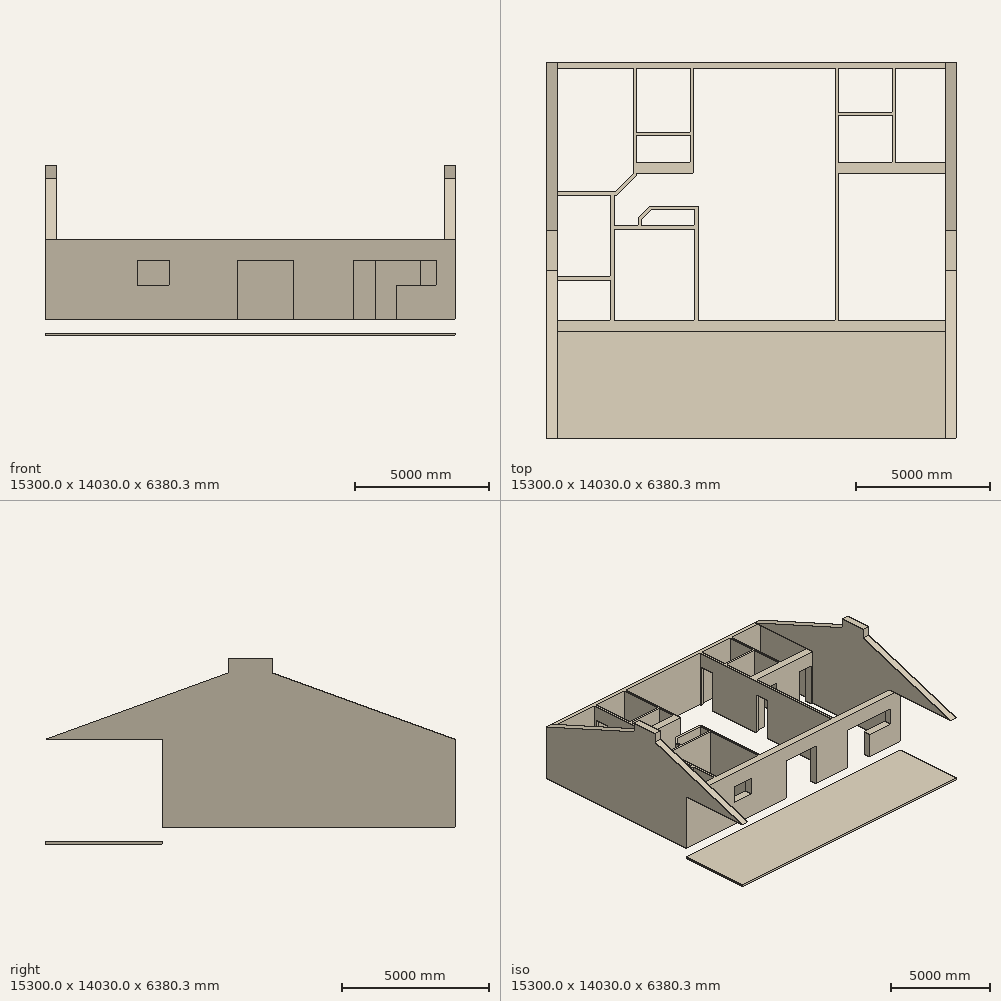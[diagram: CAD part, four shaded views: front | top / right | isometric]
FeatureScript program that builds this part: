
annotation { "Feature Type Name" : "Feature", "Feature Type Description" : "" }
export const myFeature = defineFeature(function(context is Context, id is Id, definition is map)
    precondition{}
    {
        {
            var Q0;
            Q0=qCreatedBy(makeId("Top.planeOp"),FACE);
            var sketch = newSketch(context, id + "F0", { "sketchPlane" : qUnion([Q0])});
            skLineSegment(sketch, "E0.left", {"start": v(-400, 5900) * mm, "end": v(-400, 400) * mm});
            skLineSegment(sketch, "E0.right", {"start": v(-14900, 6300) * mm, "end": v(-14900, 5200) * mm});
            skLineSegment(sketch, "E1.top", {"start": v(0, 0) * mm, "end": v(-6035, 0) * mm});
            skLineSegment(sketch, "E1.right", {"start": v(-15300, 6300) * mm, "end": v(-15300, 0) * mm});
            skLineSegment(sketch, "E2", {"start": v(0, 0) * mm, "end": v(0, 10030) * mm});
            skLineSegment(sketch, "E3", {"start": v(0, 10030) * mm, "end": v(-15300, 10030) * mm});
            skLineSegment(sketch, "E4", {"start": v(-15300, 10030) * mm, "end": v(-15300, 6300) * mm});
            skLineSegment(sketch, "E5", {"start": v(-15070, 6300) * mm, "end": v(-15070, 9800) * mm});
            skLineSegment(sketch, "E6", {"start": v(-230, 9800) * mm, "end": v(-230, 6300) * mm});
            skLineSegment(sketch, "E7.trimOffspring", {"start": v(-400, 5900) * mm, "end": v(-500, 5900) * mm});
            skLineSegment(sketch, "E8.trimOffspring", {"start": v(-230, 6300) * mm, "end": v(-500, 6300) * mm});
            skLineSegment(sketch, "E9.trimOffspring", {"start": v(-400, 400) * mm, "end": v(-4400, 400) * mm});
            skLineSegment(sketch, "E10", {"start": v(-15070, 9800) * mm, "end": v(-12070, 9800) * mm});
            skLineSegment(sketch, "E11", {"start": v(-4530, 400) * mm, "end": v(-4530, 5000) * mm});
            skLineSegment(sketch, "E12", {"start": v(-4400, 400) * mm, "end": v(-4400, 5000) * mm});
            skLineSegment(sketch, "E13", {"start": v(-2270, 6300) * mm, "end": v(-2270, 9800) * mm});
            skLineSegment(sketch, "E14", {"start": v(-2400, 6300) * mm, "end": v(-2400, 8050) * mm});
            skLineSegment(sketch, "E15", {"start": v(-4400, 6300) * mm, "end": v(-4400, 8050) * mm});
            skLineSegment(sketch, "E16", {"start": v(-4530, 5900) * mm, "end": v(-4530, 8900) * mm});
            skLineSegment(sketch, "E17", {"start": v(-4400, 8180) * mm, "end": v(-2400, 8180) * mm});
            skLineSegment(sketch, "E18", {"start": v(-4400, 8050) * mm, "end": v(-2400, 8050) * mm});
            skLineSegment(sketch, "E19", {"start": v(-12770, 400) * mm, "end": v(-12770, 500) * mm});
            skLineSegment(sketch, "E20", {"start": v(-12770, 3800) * mm, "end": v(-12670, 3800) * mm});
            skLineSegment(sketch, "E21", {"start": v(-9770, 3800) * mm, "end": v(-9770, 400) * mm});
            skLineSegment(sketch, "E22", {"start": v(-11940, 9800) * mm, "end": v(-11940, 9700) * mm});
            skLineSegment(sketch, "E23", {"start": v(-12070, 9800) * mm, "end": v(-12070, 9700) * mm});
            skLineSegment(sketch, "E24", {"start": v(-14900, 5070) * mm, "end": v(-12900, 5070) * mm});
            skLineSegment(sketch, "E25", {"start": v(-12652.55, 5070) * mm, "end": v(-12579.12, 5143.43) * mm});
            skLineSegment(sketch, "E26", {"start": v(-11940, 5782.55) * mm, "end": v(-11940, 5900) * mm});
            skLineSegment(sketch, "E27", {"start": v(-9640, 400) * mm, "end": v(-9640, 3930) * mm});
            skLineSegment(sketch, "E28", {"start": v(-9770, 3930) * mm, "end": v(-11740, 3930) * mm});
            skLineSegment(sketch, "E29", {"start": v(-12900, 3930) * mm, "end": v(-12900, 2030) * mm});
            skLineSegment(sketch, "E30", {"start": v(-9640, 3930) * mm, "end": v(-9640, 4660) * mm});
            skLineSegment(sketch, "E31", {"start": v(-9640, 4660) * mm, "end": v(-9780.34, 4660) * mm});
            skLineSegment(sketch, "E32", {"start": v(-11450.34, 4660) * mm, "end": v(-11870, 4240.34) * mm});
            skLineSegment(sketch, "E33", {"start": v(-11870, 4240.34) * mm, "end": v(-11870, 3800) * mm});
            skLineSegment(sketch, "E34", {"start": v(-11740, 3930) * mm, "end": v(-11740, 4186.5) * mm});
            skLineSegment(sketch, "E35", {"start": v(-11740, 4186.5) * mm, "end": v(-11396.5, 4530) * mm});
            skLineSegment(sketch, "E36", {"start": v(-11396.5, 4530) * mm, "end": v(-11380.34, 4530) * mm});
            skLineSegment(sketch, "E37", {"start": v(-9770, 4530) * mm, "end": v(-9770, 3930) * mm});
            skLineSegment(sketch, "E38", {"start": v(-12070, 6300) * mm, "end": v(-12070, 5836.4) * mm});
            skLineSegment(sketch, "E39", {"start": v(-12070, 5836.4) * mm, "end": v(-12105.36, 5801.04) * mm});
            skLineSegment(sketch, "E40", {"start": v(-12706.4, 5200) * mm, "end": v(-14900, 5200) * mm});
            skLineSegment(sketch, "E41", {"start": v(-9940, 6300) * mm, "end": v(-9940, 7300) * mm});
            skLineSegment(sketch, "E42", {"start": v(-9810, 5900) * mm, "end": v(-9810, 9800) * mm});
            skLineSegment(sketch, "E43", {"start": v(-11940, 7430) * mm, "end": v(-9940, 7430) * mm});
            skLineSegment(sketch, "E44", {"start": v(-11940, 7300) * mm, "end": v(-9940, 7300) * mm});
            skLineSegment(sketch, "E45", {"start": v(-12900, 2030) * mm, "end": v(-14900, 2030) * mm});
            skLineSegment(sketch, "E46", {"start": v(-12900, 1900) * mm, "end": v(-14900, 1900) * mm});
            skLineSegment(sketch, "E47.trimOffspring", {"start": v(-4400, 8180) * mm, "end": v(-4400, 8900) * mm});
            skLineSegment(sketch, "E48.trimOffspring", {"start": v(-9810, 5900) * mm, "end": v(-11140, 5900) * mm});
            skLineSegment(sketch, "E49.trimOffspring", {"start": v(-2400, 8180) * mm, "end": v(-2400, 9800) * mm});
            skLineSegment(sketch, "E50.trimOffspring", {"start": v(-4400, 9800) * mm, "end": v(-2400, 9800) * mm});
            skLineSegment(sketch, "E51.trimOffspring", {"start": v(-2270, 9800) * mm, "end": v(-230, 9800) * mm});
            skLineSegment(sketch, "E52.trimOffspring", {"start": v(-2400, 6300) * mm, "end": v(-3000, 6300) * mm});
            skLineSegment(sketch, "E53.trimOffspring", {"start": v(-4530, 400) * mm, "end": v(-6035, 400) * mm});
            skLineSegment(sketch, "E54.trimOffspring", {"start": v(-12900, 1900) * mm, "end": v(-12900, 1300) * mm});
            skLineSegment(sketch, "E55.trimOffspring", {"start": v(-14900, 1900) * mm, "end": v(-14900, 400) * mm});
            skLineSegment(sketch, "E56.trimOffspring", {"start": v(-12900, 400) * mm, "end": v(-14900, 400) * mm});
            skLineSegment(sketch, "E57.trimOffspring", {"start": v(-9770, 400) * mm, "end": v(-12770, 400) * mm});
            skLineSegment(sketch, "E58.trimOffspring", {"start": v(-14900, 5070) * mm, "end": v(-14900, 2030) * mm});
            skLineSegment(sketch, "E59.trimOffspring", {"start": v(-14900, 6300) * mm, "end": v(-15070, 6300) * mm});
            skLineSegment(sketch, "E60.trimOffspring", {"start": v(-9940, 6300) * mm, "end": v(-11140, 6300) * mm});
            skLineSegment(sketch, "E61.trimOffspring", {"start": v(-11940, 7300) * mm, "end": v(-11940, 5900) * mm});
            skLineSegment(sketch, "E62.trimOffspring", {"start": v(-9940, 7430) * mm, "end": v(-9940, 9800) * mm});
            skLineSegment(sketch, "E63.trimOffspring", {"start": v(-9810, 9800) * mm, "end": v(-4530, 9800) * mm});
            skLineSegment(sketch, "E64.trimOffspring", {"start": v(-11940, 9800) * mm, "end": v(-9940, 9800) * mm});
            skLineSegment(sketch, "E65", {"start": v(-11140, 6300) * mm, "end": v(-11140, 5900) * mm});
            skLineSegment(sketch, "E66", {"start": v(-12900, 5070) * mm, "end": v(-12900, 4730) * mm});
            skLineSegment(sketch, "E67", {"start": v(-12900, 4730) * mm, "end": v(-12770, 4730) * mm});
            skLineSegment(sketch, "E68", {"start": v(-12770, 4730) * mm, "end": v(-12770, 5070) * mm});
            skLineSegment(sketch, "E69.trimOffspring", {"start": v(-12770, 5070) * mm, "end": v(-12652.55, 5070) * mm});
            skLineSegment(sketch, "E70", {"start": v(-12670, 3930) * mm, "end": v(-12670, 3800) * mm});
            skLineSegment(sketch, "E71.trimOffspring", {"start": v(-12670, 3930) * mm, "end": v(-12900, 3930) * mm});
            skLineSegment(sketch, "E72.trimOffspring", {"start": v(-11870, 3800) * mm, "end": v(-9770, 3800) * mm});
            skPoint(sketch, "E73.trimOffspring.start.orphan", {"position": v(-12070, 5900) * mm});
            skLineSegment(sketch, "E74", {"start": v(-12105.36, 5801.04) * mm, "end": v(-12013.43, 5709.12) * mm});
            skLineSegment(sketch, "E75", {"start": v(-12671.04, 5235.36) * mm, "end": v(-12579.12, 5143.43) * mm});
            skLineSegment(sketch, "E76.trimOffspring", {"start": v(-12671.04, 5235.36) * mm, "end": v(-12706.4, 5200) * mm});
            skLineSegment(sketch, "E77.trimOffspring", {"start": v(-12013.43, 5709.12) * mm, "end": v(-11940, 5782.55) * mm});
            skLineSegment(sketch, "E78", {"start": v(-12900, 500) * mm, "end": v(-12770, 500) * mm});
            skLineSegment(sketch, "E79", {"start": v(-12900, 1300) * mm, "end": v(-12770, 1300) * mm});
            skLineSegment(sketch, "E80.trimOffspring", {"start": v(-12900, 500) * mm, "end": v(-12900, 400) * mm});
            skLineSegment(sketch, "E81.trimOffspring", {"start": v(-12770, 1300) * mm, "end": v(-12770, 3800) * mm});
            skLineSegment(sketch, "E82", {"start": v(-12070, 9700) * mm, "end": v(-11940, 9700) * mm});
            skLineSegment(sketch, "E83", {"start": v(-12070, 8900) * mm, "end": v(-11940, 8900) * mm});
            skLineSegment(sketch, "E84.trimOffspring", {"start": v(-12070, 8900) * mm, "end": v(-12070, 6300) * mm});
            skLineSegment(sketch, "E85.trimOffspring", {"start": v(-11940, 8900) * mm, "end": v(-11940, 7430) * mm});
            skLineSegment(sketch, "E86", {"start": v(-4530, 9700) * mm, "end": v(-4400, 9700) * mm});
            skLineSegment(sketch, "E87", {"start": v(-4530, 8900) * mm, "end": v(-4400, 8900) * mm});
            skLineSegment(sketch, "E88", {"start": v(-3800, 6300) * mm, "end": v(-3800, 5900) * mm});
            skLineSegment(sketch, "E89", {"start": v(-3000, 6300) * mm, "end": v(-3000, 5900) * mm});
            skLineSegment(sketch, "E90", {"start": v(-1300, 6300) * mm, "end": v(-1300, 5900) * mm});
            skLineSegment(sketch, "E91", {"start": v(-500, 6300) * mm, "end": v(-500, 5900) * mm});
            skLineSegment(sketch, "E92.trimOffspring", {"start": v(-1300, 6300) * mm, "end": v(-2270, 6300) * mm});
            skLineSegment(sketch, "E93.trimOffspring", {"start": v(-1300, 5900) * mm, "end": v(-3000, 5900) * mm});
            skLineSegment(sketch, "E94.trimOffspring", {"start": v(-3800, 6300) * mm, "end": v(-4400, 6300) * mm});
            skLineSegment(sketch, "E95.trimOffspring", {"start": v(-3800, 5900) * mm, "end": v(-4400, 5900) * mm});
            skLineSegment(sketch, "E96.trimOffspring", {"start": v(-4530, 9700) * mm, "end": v(-4530, 9800) * mm});
            skLineSegment(sketch, "E97.trimOffspring", {"start": v(-4400, 9700) * mm, "end": v(-4400, 9800) * mm});
            skLineSegment(sketch, "E98", {"start": v(-4530, 5800) * mm, "end": v(-4400, 5800) * mm});
            skLineSegment(sketch, "E99", {"start": v(-4530, 5000) * mm, "end": v(-4400, 5000) * mm});
            skLineSegment(sketch, "E100.trimOffspring", {"start": v(-4530, 5800) * mm, "end": v(-4530, 5900) * mm});
            skLineSegment(sketch, "E101.trimOffspring", {"start": v(-4400, 5800) * mm, "end": v(-4400, 5900) * mm});
            skLineSegment(sketch, "E102", {"start": v(-11380.34, 4660) * mm, "end": v(-11380.34, 4530) * mm});
            skLineSegment(sketch, "E103", {"start": v(-9780.34, 4660) * mm, "end": v(-9780.34, 4530) * mm});
            skLineSegment(sketch, "E104.trimOffspring", {"start": v(-11380.34, 4660) * mm, "end": v(-11450.34, 4660) * mm});
            skLineSegment(sketch, "E105.trimOffspring", {"start": v(-9780.34, 4530) * mm, "end": v(-9770, 4530) * mm});
            skLineSegment(sketch, "E106", {"start": v(-8135, 400) * mm, "end": v(-8135, 0) * mm});
            skLineSegment(sketch, "E107", {"start": v(-6035, 400) * mm, "end": v(-6035, 0) * mm});
            skLineSegment(sketch, "E108.trimOffspring", {"start": v(-8135, 400) * mm, "end": v(-9640, 400) * mm});
            skLineSegment(sketch, "E109.trimOffspring", {"start": v(-8135, 0) * mm, "end": v(-15300, 0) * mm});
            skSolve(sketch);
        }
        {
            var Q0;
            Q0 = qSketchRegion(id + "F0", true);
            extrude(context, id + "F1", {"entities" : qUnion([Q0]), "depth" : 2200 * mm, "offsetDistance" : 25 * mm});
        }
        {
            var Q0;
            Q0=makeQuery(id+"F1.opExtrude","CAP_FACE",FACE,{"disambiguationData":[OSD([sQuery(id+"F0.wireOp",EDGE,"E0.left"),sQuery(id+"F0.wireOp",EDGE,"E0.right"),sQuery(id+"F0.wireOp",EDGE,"E1.top"),sQuery(id+"F0.wireOp",EDGE,"E1.right"),sQuery(id+"F0.wireOp",EDGE,"E2"),sQuery(id+"F0.wireOp",EDGE,"E3"),sQuery(id+"F0.wireOp",EDGE,"E4"),sQuery(id+"F0.wireOp",EDGE,"E5"),sQuery(id+"F0.wireOp",EDGE,"E6"),sQuery(id+"F0.wireOp",EDGE,"E7.trimOffspring"),sQuery(id+"F0.wireOp",EDGE,"E8.trimOffspring"),sQuery(id+"F0.wireOp",EDGE,"E9.trimOffspring"),sQuery(id+"F0.wireOp",EDGE,"E10"),sQuery(id+"F0.wireOp",EDGE,"E11"),sQuery(id+"F0.wireOp",EDGE,"E12"),sQuery(id+"F0.wireOp",EDGE,"E13"),sQuery(id+"F0.wireOp",EDGE,"E14"),sQuery(id+"F0.wireOp",EDGE,"E15"),sQuery(id+"F0.wireOp",EDGE,"E16"),sQuery(id+"F0.wireOp",EDGE,"E17"),sQuery(id+"F0.wireOp",EDGE,"E18"),sQuery(id+"F0.wireOp",EDGE,"E19"),sQuery(id+"F0.wireOp",EDGE,"E20"),sQuery(id+"F0.wireOp",EDGE,"E21"),sQuery(id+"F0.wireOp",EDGE,"E22"),sQuery(id+"F0.wireOp",EDGE,"E23"),sQuery(id+"F0.wireOp",EDGE,"E24"),sQuery(id+"F0.wireOp",EDGE,"E25"),sQuery(id+"F0.wireOp",EDGE,"E26"),sQuery(id+"F0.wireOp",EDGE,"E27"),sQuery(id+"F0.wireOp",EDGE,"E28"),sQuery(id+"F0.wireOp",EDGE,"E29"),sQuery(id+"F0.wireOp",EDGE,"E30"),sQuery(id+"F0.wireOp",EDGE,"E31"),sQuery(id+"F0.wireOp",EDGE,"E32"),sQuery(id+"F0.wireOp",EDGE,"E33"),sQuery(id+"F0.wireOp",EDGE,"E34"),sQuery(id+"F0.wireOp",EDGE,"E35"),sQuery(id+"F0.wireOp",EDGE,"E36"),sQuery(id+"F0.wireOp",EDGE,"E37"),sQuery(id+"F0.wireOp",EDGE,"E38"),sQuery(id+"F0.wireOp",EDGE,"E39"),sQuery(id+"F0.wireOp",EDGE,"E40"),sQuery(id+"F0.wireOp",EDGE,"E41"),sQuery(id+"F0.wireOp",EDGE,"E42"),sQuery(id+"F0.wireOp",EDGE,"E43"),sQuery(id+"F0.wireOp",EDGE,"E44"),sQuery(id+"F0.wireOp",EDGE,"E45"),sQuery(id+"F0.wireOp",EDGE,"E46"),sQuery(id+"F0.wireOp",EDGE,"E47.trimOffspring"),sQuery(id+"F0.wireOp",EDGE,"E48.trimOffspring"),sQuery(id+"F0.wireOp",EDGE,"E49.trimOffspring"),sQuery(id+"F0.wireOp",EDGE,"E50.trimOffspring"),sQuery(id+"F0.wireOp",EDGE,"E51.trimOffspring"),sQuery(id+"F0.wireOp",EDGE,"E52.trimOffspring"),sQuery(id+"F0.wireOp",EDGE,"E53.trimOffspring"),sQuery(id+"F0.wireOp",EDGE,"E54.trimOffspring"),sQuery(id+"F0.wireOp",EDGE,"E55.trimOffspring"),sQuery(id+"F0.wireOp",EDGE,"E56.trimOffspring"),sQuery(id+"F0.wireOp",EDGE,"E57.trimOffspring"),sQuery(id+"F0.wireOp",EDGE,"E58.trimOffspring"),sQuery(id+"F0.wireOp",EDGE,"E59.trimOffspring"),sQuery(id+"F0.wireOp",EDGE,"E60.trimOffspring"),sQuery(id+"F0.wireOp",EDGE,"E61.trimOffspring"),sQuery(id+"F0.wireOp",EDGE,"E62.trimOffspring"),sQuery(id+"F0.wireOp",EDGE,"E63.trimOffspring"),sQuery(id+"F0.wireOp",EDGE,"E64.trimOffspring"),sQuery(id+"F0.wireOp",EDGE,"E65"),sQuery(id+"F0.wireOp",EDGE,"E66"),sQuery(id+"F0.wireOp",EDGE,"E67"),sQuery(id+"F0.wireOp",EDGE,"E68"),sQuery(id+"F0.wireOp",EDGE,"E69.trimOffspring"),sQuery(id+"F0.wireOp",EDGE,"E70"),sQuery(id+"F0.wireOp",EDGE,"E71.trimOffspring"),sQuery(id+"F0.wireOp",EDGE,"E72.trimOffspring"),sQuery(id+"F0.wireOp",EDGE,"E74"),sQuery(id+"F0.wireOp",EDGE,"E75"),sQuery(id+"F0.wireOp",EDGE,"E76.trimOffspring"),sQuery(id+"F0.wireOp",EDGE,"E77.trimOffspring"),sQuery(id+"F0.wireOp",EDGE,"E78"),sQuery(id+"F0.wireOp",EDGE,"E79"),sQuery(id+"F0.wireOp",EDGE,"E80.trimOffspring"),sQuery(id+"F0.wireOp",EDGE,"E81.trimOffspring"),sQuery(id+"F0.wireOp",EDGE,"E82"),sQuery(id+"F0.wireOp",EDGE,"E83"),sQuery(id+"F0.wireOp",EDGE,"E84.trimOffspring"),sQuery(id+"F0.wireOp",EDGE,"E85.trimOffspring"),sQuery(id+"F0.wireOp",EDGE,"E86"),sQuery(id+"F0.wireOp",EDGE,"E87"),sQuery(id+"F0.wireOp",EDGE,"E88"),sQuery(id+"F0.wireOp",EDGE,"E89"),sQuery(id+"F0.wireOp",EDGE,"E90"),sQuery(id+"F0.wireOp",EDGE,"E91"),sQuery(id+"F0.wireOp",EDGE,"E92.trimOffspring"),sQuery(id+"F0.wireOp",EDGE,"E93.trimOffspring"),sQuery(id+"F0.wireOp",EDGE,"E94.trimOffspring"),sQuery(id+"F0.wireOp",EDGE,"E95.trimOffspring"),sQuery(id+"F0.wireOp",EDGE,"E96.trimOffspring"),sQuery(id+"F0.wireOp",EDGE,"E97.trimOffspring"),sQuery(id+"F0.wireOp",EDGE,"E98"),sQuery(id+"F0.wireOp",EDGE,"E99"),sQuery(id+"F0.wireOp",EDGE,"E100.trimOffspring"),sQuery(id+"F0.wireOp",EDGE,"E101.trimOffspring"),sQuery(id+"F0.wireOp",EDGE,"E102"),sQuery(id+"F0.wireOp",EDGE,"E103"),sQuery(id+"F0.wireOp",EDGE,"E104.trimOffspring"),sQuery(id+"F0.wireOp",EDGE,"E105.trimOffspring"),sQuery(id+"F0.wireOp",EDGE,"E106"),sQuery(id+"F0.wireOp",EDGE,"E107"),sQuery(id+"F0.wireOp",EDGE,"E108.trimOffspring"),sQuery(id+"F0.wireOp",EDGE,"E109.trimOffspring")])],"isStart":false});
            var sketch = newSketch(context, id + "F2", { "sketchPlane" : qUnion([Q0])});
            skLineSegment(sketch, "E110.0", {"start": v(-400, 5900) * mm, "end": v(-400, 400) * mm});
            skLineSegment(sketch, "E110.1", {"start": v(-14900, 6300) * mm, "end": v(-14900, 5200) * mm});
            skLineSegment(sketch, "E110.2", {"start": v(0, 0) * mm, "end": v(-6035, 0) * mm});
            skLineSegment(sketch, "E110.3", {"start": v(-15300, 6300) * mm, "end": v(-15300, 0) * mm});
            skLineSegment(sketch, "E110.4", {"start": v(0, 0) * mm, "end": v(0, 10030) * mm});
            skLineSegment(sketch, "E110.5", {"start": v(0, 10030) * mm, "end": v(-15300, 10030) * mm});
            skLineSegment(sketch, "E110.6", {"start": v(-15300, 10030) * mm, "end": v(-15300, 6300) * mm});
            skLineSegment(sketch, "E110.7", {"start": v(-15070, 6300) * mm, "end": v(-15070, 9800) * mm});
            skLineSegment(sketch, "E110.8", {"start": v(-230, 9800) * mm, "end": v(-230, 6300) * mm});
            skLineSegment(sketch, "E110.9", {"start": v(-400, 5900) * mm, "end": v(-500, 5900) * mm});
            skLineSegment(sketch, "E110.10", {"start": v(-230, 6300) * mm, "end": v(-500, 6300) * mm});
            skLineSegment(sketch, "E110.11", {"start": v(-400, 400) * mm, "end": v(-4400, 400) * mm});
            skLineSegment(sketch, "E110.12", {"start": v(-15070, 9800) * mm, "end": v(-12070, 9800) * mm});
            skLineSegment(sketch, "E110.13", {"start": v(-4530, 400) * mm, "end": v(-4530, 5800) * mm});
            skLineSegment(sketch, "E110.14", {"start": v(-4400, 400) * mm, "end": v(-4400, 5800) * mm});
            skLineSegment(sketch, "E110.15", {"start": v(-2270, 6300) * mm, "end": v(-2270, 9800) * mm});
            skLineSegment(sketch, "E110.16", {"start": v(-2400, 6300) * mm, "end": v(-2400, 8050) * mm});
            skLineSegment(sketch, "E110.17", {"start": v(-4400, 6300) * mm, "end": v(-4400, 8050) * mm});
            skLineSegment(sketch, "E110.18", {"start": v(-4530, 5900) * mm, "end": v(-4530, 9700) * mm});
            skLineSegment(sketch, "E110.19", {"start": v(-4400, 8180) * mm, "end": v(-2400, 8180) * mm});
            skLineSegment(sketch, "E110.20", {"start": v(-4400, 8050) * mm, "end": v(-2400, 8050) * mm});
            skLineSegment(sketch, "E110.21", {"start": v(-12770, 400) * mm, "end": v(-12770, 500) * mm});
            skLineSegment(sketch, "E110.22", {"start": v(-12770, 3800) * mm, "end": v(-11870, 3800) * mm});
            skLineSegment(sketch, "E110.23", {"start": v(-9770, 3800) * mm, "end": v(-9770, 400) * mm});
            skLineSegment(sketch, "E110.24", {"start": v(-11940, 9800) * mm, "end": v(-11940, 9700) * mm});
            skLineSegment(sketch, "E110.25", {"start": v(-12070, 9800) * mm, "end": v(-12070, 9700) * mm});
            skLineSegment(sketch, "E110.26", {"start": v(-14900, 5070) * mm, "end": v(-12900, 5070) * mm});
            skLineSegment(sketch, "E110.27", {"start": v(-12652.55, 5070) * mm, "end": v(-12013.43, 5709.12) * mm});
            skLineSegment(sketch, "E110.28", {"start": v(-11940, 5782.55) * mm, "end": v(-11940, 5900) * mm});
            skLineSegment(sketch, "E110.29", {"start": v(-9640, 400) * mm, "end": v(-9640, 3930) * mm});
            skLineSegment(sketch, "E110.30", {"start": v(-9770, 3930) * mm, "end": v(-11740, 3930) * mm});
            skLineSegment(sketch, "E110.31", {"start": v(-12900, 3930) * mm, "end": v(-12900, 2030) * mm});
            skLineSegment(sketch, "E110.32", {"start": v(-9640, 3930) * mm, "end": v(-9640, 4660) * mm});
            skLineSegment(sketch, "E110.33", {"start": v(-9640, 4660) * mm, "end": v(-9780.34, 4660) * mm});
            skLineSegment(sketch, "E110.34", {"start": v(-11450.34, 4660) * mm, "end": v(-11870, 4240.34) * mm});
            skLineSegment(sketch, "E110.35", {"start": v(-11870, 4240.34) * mm, "end": v(-11870, 3930) * mm});
            skLineSegment(sketch, "E110.36", {"start": v(-11740, 3930) * mm, "end": v(-11740, 4186.5) * mm});
            skLineSegment(sketch, "E110.37", {"start": v(-11740, 4186.5) * mm, "end": v(-11396.5, 4530) * mm});
            skLineSegment(sketch, "E110.38", {"start": v(-11396.5, 4530) * mm, "end": v(-9780.34, 4530) * mm});
            skLineSegment(sketch, "E110.39", {"start": v(-9770, 4530) * mm, "end": v(-9770, 3930) * mm});
            skLineSegment(sketch, "E110.40", {"start": v(-12070, 6300) * mm, "end": v(-12070, 5836.4) * mm});
            skLineSegment(sketch, "E110.41", {"start": v(-12070, 5836.4) * mm, "end": v(-12105.36, 5801.04) * mm});
            skLineSegment(sketch, "E110.42", {"start": v(-12706.4, 5200) * mm, "end": v(-14900, 5200) * mm});
            skLineSegment(sketch, "E110.43", {"start": v(-9940, 6300) * mm, "end": v(-9940, 7300) * mm});
            skLineSegment(sketch, "E110.44", {"start": v(-9810, 5900) * mm, "end": v(-9810, 9800) * mm});
            skLineSegment(sketch, "E110.45", {"start": v(-11940, 7430) * mm, "end": v(-9940, 7430) * mm});
            skLineSegment(sketch, "E110.46", {"start": v(-11940, 7300) * mm, "end": v(-9940, 7300) * mm});
            skLineSegment(sketch, "E110.47", {"start": v(-12900, 2030) * mm, "end": v(-14900, 2030) * mm});
            skLineSegment(sketch, "E110.48", {"start": v(-12900, 1900) * mm, "end": v(-14900, 1900) * mm});
            skLineSegment(sketch, "E110.49", {"start": v(-4400, 8180) * mm, "end": v(-4400, 9700) * mm});
            skLineSegment(sketch, "E110.50", {"start": v(-9810, 5900) * mm, "end": v(-11940, 5900) * mm});
            skLineSegment(sketch, "E110.51", {"start": v(-2400, 8180) * mm, "end": v(-2400, 9800) * mm});
            skLineSegment(sketch, "E110.52", {"start": v(-4400, 9800) * mm, "end": v(-2400, 9800) * mm});
            skLineSegment(sketch, "E110.53", {"start": v(-2270, 9800) * mm, "end": v(-230, 9800) * mm});
            skLineSegment(sketch, "E110.54", {"start": v(-2400, 6300) * mm, "end": v(-3000, 6300) * mm});
            skLineSegment(sketch, "E110.55", {"start": v(-4530, 400) * mm, "end": v(-6035, 400) * mm});
            skLineSegment(sketch, "E110.56", {"start": v(-12900, 1900) * mm, "end": v(-12900, 500) * mm});
            skLineSegment(sketch, "E110.57", {"start": v(-14900, 1900) * mm, "end": v(-14900, 400) * mm});
            skLineSegment(sketch, "E110.58", {"start": v(-12900, 400) * mm, "end": v(-14900, 400) * mm});
            skLineSegment(sketch, "E110.59", {"start": v(-9770, 400) * mm, "end": v(-12770, 400) * mm});
            skLineSegment(sketch, "E110.60", {"start": v(-14900, 5070) * mm, "end": v(-14900, 2030) * mm});
            skLineSegment(sketch, "E110.61", {"start": v(-14900, 6300) * mm, "end": v(-15070, 6300) * mm});
            skLineSegment(sketch, "E110.62", {"start": v(-9940, 6300) * mm, "end": v(-11940, 6300) * mm});
            skLineSegment(sketch, "E110.63", {"start": v(-11940, 7300) * mm, "end": v(-11940, 6300) * mm});
            skLineSegment(sketch, "E110.64", {"start": v(-9940, 7430) * mm, "end": v(-9940, 9800) * mm});
            skLineSegment(sketch, "E110.65", {"start": v(-9810, 9800) * mm, "end": v(-4530, 9800) * mm});
            skLineSegment(sketch, "E110.66", {"start": v(-11940, 9800) * mm, "end": v(-9940, 9800) * mm});
            skLineSegment(sketch, "E110.68", {"start": v(-12900, 5070) * mm, "end": v(-12900, 3930) * mm});
            skLineSegment(sketch, "E110.70", {"start": v(-12770, 3930) * mm, "end": v(-12770, 5070) * mm});
            skLineSegment(sketch, "E110.71", {"start": v(-12770, 5070) * mm, "end": v(-12652.55, 5070) * mm});
            skLineSegment(sketch, "E110.73", {"start": v(-11870, 3930) * mm, "end": v(-12770, 3930) * mm});
            skLineSegment(sketch, "E110.74", {"start": v(-11870, 3800) * mm, "end": v(-9770, 3800) * mm});
            skPoint(sketch, "E110.75", {"position": v(-12070, 5900) * mm});
            skLineSegment(sketch, "E110.78", {"start": v(-12105.36, 5801.04) * mm, "end": v(-12706.4, 5200) * mm});
            skLineSegment(sketch, "E110.79", {"start": v(-12013.43, 5709.12) * mm, "end": v(-11940, 5782.55) * mm});
            skLineSegment(sketch, "E110.82", {"start": v(-12900, 500) * mm, "end": v(-12900, 400) * mm});
            skLineSegment(sketch, "E110.83", {"start": v(-12770, 500) * mm, "end": v(-12770, 3800) * mm});
            skLineSegment(sketch, "E110.86", {"start": v(-12070, 9700) * mm, "end": v(-12070, 6300) * mm});
            skLineSegment(sketch, "E110.87", {"start": v(-11940, 9700) * mm, "end": v(-11940, 7430) * mm});
            skLineSegment(sketch, "E110.94", {"start": v(-500, 6300) * mm, "end": v(-2270, 6300) * mm});
            skLineSegment(sketch, "E110.95", {"start": v(-500, 5900) * mm, "end": v(-3000, 5900) * mm});
            skLineSegment(sketch, "E110.96", {"start": v(-3000, 6300) * mm, "end": v(-4400, 6300) * mm});
            skLineSegment(sketch, "E110.97", {"start": v(-3000, 5900) * mm, "end": v(-4400, 5900) * mm});
            skLineSegment(sketch, "E110.98", {"start": v(-4530, 9700) * mm, "end": v(-4530, 9800) * mm});
            skLineSegment(sketch, "E110.99", {"start": v(-4400, 9700) * mm, "end": v(-4400, 9800) * mm});
            skLineSegment(sketch, "E110.102", {"start": v(-4530, 5800) * mm, "end": v(-4530, 5900) * mm});
            skLineSegment(sketch, "E110.103", {"start": v(-4400, 5800) * mm, "end": v(-4400, 5900) * mm});
            skLineSegment(sketch, "E110.106", {"start": v(-9780.34, 4660) * mm, "end": v(-11450.34, 4660) * mm});
            skLineSegment(sketch, "E110.107", {"start": v(-9780.34, 4530) * mm, "end": v(-9770, 4530) * mm});
            skLineSegment(sketch, "E110.110", {"start": v(-6035, 400) * mm, "end": v(-9640, 400) * mm});
            skLineSegment(sketch, "E110.111", {"start": v(-6035, 0) * mm, "end": v(-15300, 0) * mm});
            skPoint(sketch, "E111.orphan", {"position": v(-4530, 8900) * mm});
            skPoint(sketch, "E112.orphan", {"position": v(-4400, 8900) * mm});
            skPoint(sketch, "E113.orphan", {"position": v(-3800, 6300) * mm});
            skPoint(sketch, "E114.orphan", {"position": v(-3800, 5900) * mm});
            skPoint(sketch, "E115.orphan", {"position": v(-4530, 5000) * mm});
            skPoint(sketch, "E116.orphan", {"position": v(-4400, 5000) * mm});
            skPoint(sketch, "E117.orphan", {"position": v(-1300, 6300) * mm});
            skPoint(sketch, "E118.orphan", {"position": v(-1300, 5900) * mm});
            skPoint(sketch, "E119.orphan", {"position": v(-12770, 1300) * mm});
            skPoint(sketch, "E120.orphan", {"position": v(-12900, 1300) * mm});
            skPoint(sketch, "E121.orphan", {"position": v(-11380.34, 4660) * mm});
            skPoint(sketch, "E122.orphan", {"position": v(-11380.34, 4530) * mm});
            skPoint(sketch, "E123.orphan", {"position": v(-12770, 4730) * mm});
            skPoint(sketch, "E124.orphan", {"position": v(-12900, 4730) * mm});
            skPoint(sketch, "E125.orphan", {"position": v(-11140, 6300) * mm});
            skPoint(sketch, "E126.orphan", {"position": v(-11140, 5900) * mm});
            skPoint(sketch, "E127.orphan", {"position": v(-12070, 8900) * mm});
            skPoint(sketch, "E128.orphan", {"position": v(-11940, 8900) * mm});
            skPoint(sketch, "E110.77.end.orphan", {"position": v(-12579.12, 5143.43) * mm});
            skPoint(sketch, "E110.77.start.orphan", {"position": v(-12671.04, 5235.36) * mm});
            skPoint(sketch, "E110.72.end.orphan", {"position": v(-12670, 3800) * mm});
            skPoint(sketch, "E110.72.start.orphan", {"position": v(-12670, 3930) * mm});
            skPoint(sketch, "E129.orphan", {"position": v(-11870, 3800) * mm});
            skPoint(sketch, "E110.109.end.orphan", {"position": v(-6035, 0) * mm});
            skPoint(sketch, "E110.109.start.orphan", {"position": v(-6035, 400) * mm});
            skPoint(sketch, "E110.108.end.orphan", {"position": v(-8135, 0) * mm});
            skPoint(sketch, "E110.108.start.orphan", {"position": v(-8135, 400) * mm});
            skSolve(sketch);
        }
        {
            var Q0;
            Q0 = qSketchRegion(id + "F2", true);
            extrude(context, id + "F3", {"entities" : qUnion([Q0]), "operationType" : NewBodyOperationType.ADD, "depth" : 800 * mm, "offsetDistance" : 25 * mm});
        }
        {
            var Q0;
            Q0=makeQuery(id+"F1.opExtrude","CAP_FACE",FACE,{"disambiguationData":[OSD([sQuery(id+"F0.wireOp",EDGE,"E0.bottom"),sQuery(id+"F0.wireOp",EDGE,"E0.top"),sQuery(id+"F0.wireOp",EDGE,"E0.left"),sQuery(id+"F0.wireOp",EDGE,"E0.right"),sQuery(id+"F0.wireOp",EDGE,"E1.bottom"),sQuery(id+"F0.wireOp",EDGE,"E1.top"),sQuery(id+"F0.wireOp",EDGE,"E1.left"),sQuery(id+"F0.wireOp",EDGE,"E1.right"),sQuery(id+"F0.wireOp",EDGE,"0LfAQHpO-RJrq-ou6v-1cZO-ZtXrXeZSPm6Y"),sQuery(id+"F0.wireOp",EDGE,"vXlVDgY6-Lycf-aBA6-rsYt-7ypq4eNDUVez"),sQuery(id+"F0.wireOp",EDGE,"E2"),sQuery(id+"F0.wireOp",EDGE,"E3"),sQuery(id+"F0.wireOp",EDGE,"E4"),sQuery(id+"F0.wireOp",EDGE,"E5"),sQuery(id+"F0.wireOp",EDGE,"CGNLpVIc-ITEY-u3mj-3BXb-Ykdz4nhuTWfX"),sQuery(id+"F0.wireOp",EDGE,"E6"),sQuery(id+"F0.wireOp",EDGE,"jay37AxC-18hr-6Sap-EyGX-2rZjPrXQTAcL"),sQuery(id+"F0.wireOp",EDGE,"GliK2GQi-Nw9R-AVqM-AN8O-bSjqc7BptrvE"),sQuery(id+"F0.wireOp",EDGE,"IrRdUCrI-2yr1-bYei-Oeui-EsxqEUyjUEhU"),sQuery(id+"F0.wireOp",EDGE,"0n0T1JrG-Alti-4K9V-EzRt-2c9G9PdCvcvo"),sQuery(id+"F0.wireOp",EDGE,"b8e8fed2-cb6f-4925-8fbd-82b8f5089385.trimOffspring"),sQuery(id+"F0.wireOp",EDGE,"cd91cfde-f1d4-4485-b1bd-bb38577d3c76.trimOffspring"),sQuery(id+"F0.wireOp",EDGE,"e47594a5-70bc-49a8-a4f9-902b0d1fc5c8.trimOffspring"),sQuery(id+"F0.wireOp",EDGE,"285f36d8-7a28-4fd0-9731-79a3c77a3235.trimOffspring"),sQuery(id+"F0.wireOp",EDGE,"E7.trimOffspring"),sQuery(id+"F0.wireOp",EDGE,"0c4f3d71-1864-4ebc-9790-59029a2f5197.trimOffspring")])],"isStart":true});
            var sketch = newSketch(context, id + "F4", { "sketchPlane" : qUnion([Q0])});
            skLineSegment(sketch, "E130.bottom", {"start": v(0, 0) * mm, "end": v(0, 0) * mm});
            skLineSegment(sketch, "E130.top", {"start": v(0, 4000) * mm, "end": v(0, 4000) * mm});
            skLineSegment(sketch, "E130.left", {"start": v(0, 0) * mm, "end": v(0, 4000) * mm});
            skLineSegment(sketch, "E131", {"start": v(0, 0) * mm, "end": v(-15300, 0) * mm});
            skLineSegment(sketch, "E132", {"start": v(-15300, 0) * mm, "end": v(-15300, 4000) * mm});
            skLineSegment(sketch, "E133", {"start": v(-15300, 4000) * mm, "end": v(0, 4000) * mm});
            skSolve(sketch);
        }
        {
            var Q0;
            Q0 = qSketchRegion(id + "F4", true);
            extrude(context, id + "F5", {"entities" : qUnion([Q0]), "depth" : 100 * mm, "offsetDistance" : 25 * mm});
        }
        {
            var Q0;
            Q0=makeQuery(id+"F5.opExtrude","SWEPT_BODY",BODY,{"disambiguationData":[OSD([sQuery(id+"F4.wireOp",EDGE,"E130.bottom"),sQuery(id+"F4.wireOp",EDGE,"E130.top"),sQuery(id+"F4.wireOp",EDGE,"E130.left"),sQuery(id+"F4.wireOp",EDGE,"E130.right")])]});
            var Q1;
            Q1=makeQuery(id+"F1.opExtrude","SWEPT_EDGE",EDGE,{"disambiguationData":[OSD([sQuery(id+"F0.wireOp",EDGE,"E1.top"),sQuery(id+"F0.wireOp",EDGE,"E1.left")])]});
            transform(context, id + "F6", {"entities" : qUnion([Q0]), "transformType" : TransformType.TRANSLATION_3D, "dx" : 0 * mm, "dy" : 0 * mm, "dz" : -500 * mm, "makeCopy" : false});
        }
        {
            var Q0;
            Q0=makeQuery(id+"F1.opExtrude","SWEPT_FACE",FACE,{"disambiguationData":[OSD([sQuery(id+"F0.wireOp",EDGE,"E1.left"),sQuery(id+"F0.wireOp",EDGE,"E2")])]});
            var sketch = newSketch(context, id + "F7", { "sketchPlane" : qUnion([Q0])});
            skLineSegment(sketch, "E134", {"start": v(10030, 3000) * mm, "end": v(3765, 5280.27) * mm});
            skLineSegment(sketch, "E135", {"start": v(3765, 5280.27) * mm, "end": v(3765, 5780.27) * mm});
            skLineSegment(sketch, "E136", {"start": v(3765, 5780.27) * mm, "end": v(2265, 5780.27) * mm});
            skLineSegment(sketch, "E137", {"start": v(2265, 5780.27) * mm, "end": v(2265, 5280.27) * mm});
            skLineSegment(sketch, "E138", {"start": v(2265, 5280.27) * mm, "end": v(-4000, 3000) * mm});
            skLineSegment(sketch, "E139", {"start": v(-4000, 3000) * mm, "end": v(-4000, -500) * mm, "construction": true});
            skLineSegment(sketch, "E140", {"start": v(-4000, 3000) * mm, "end": v(10030, 3000) * mm});
            skLineSegment(sketch, "E141", {"start": v(3015, 5780.27) * mm, "end": v(3015, 3000) * mm, "construction": true});
            skSolve(sketch);
        }
        {
            var Q0;
            Q0 = qSketchRegion(id + "F7", true);
            var Q1;
            Q1=makeQuery(id+"F1.opExtrude","SWEPT_FACE",FACE,{"disambiguationData":[OSD([sQuery(id+"F0.wireOp",EDGE,"E0.left")])]});
            extrude(context, id + "F8", {"entities" : qUnion([Q0]), "operationType" : NewBodyOperationType.ADD, "endBound" : BoundingType.UP_TO_SURFACE, "oppositeDirection" : true, "depth" : 25 * mm, "endBoundEntityFace" : qUnion([Q1]), "offsetDistance" : 25 * mm});
        }
        {
            var Q0;
            Q0=makeQuery(id+"F1.opExtrude","SWEPT_FACE",FACE,{"disambiguationData":[OSD([sQuery(id+"F0.wireOp",EDGE,"E1.right"),sQuery(id+"F0.wireOp",EDGE,"E4")])]});
            var sketch = newSketch(context, id + "F9", { "sketchPlane" : qUnion([Q0])});
            skLineSegment(sketch, "E142.0", {"start": v(-10030, 3000) * mm, "end": v(-3765, 5280.27) * mm});
            skLineSegment(sketch, "E142.1", {"start": v(-3765, 5280.27) * mm, "end": v(-3765, 5780.27) * mm});
            skLineSegment(sketch, "E142.2", {"start": v(-3765, 5780.27) * mm, "end": v(-2265, 5780.27) * mm});
            skLineSegment(sketch, "E142.3", {"start": v(-2265, 5780.27) * mm, "end": v(-2265, 5280.27) * mm});
            skLineSegment(sketch, "E142.4", {"start": v(-2265, 5280.27) * mm, "end": v(4000, 3000) * mm});
            skLineSegment(sketch, "E142.5", {"start": v(4000, 3000) * mm, "end": v(4000, -500) * mm});
            skLineSegment(sketch, "E142.6", {"start": v(4000, 3000) * mm, "end": v(-10030, 3000) * mm});
            skLineSegment(sketch, "E142.7", {"start": v(-3015, 5780.27) * mm, "end": v(-3015, 3000) * mm});
            skSolve(sketch);
        }
        {
            var Q0;
            Q0 = qSketchRegion(id + "F9", true);
            var Q1;
            Q1=makeQuery(id+"F1.opExtrude","SWEPT_FACE",FACE,{"disambiguationData":[OSD([sQuery(id+"F0.wireOp",EDGE,"E0.right")])]});
            extrude(context, id + "F10", {"entities" : qUnion([Q0]), "operationType" : NewBodyOperationType.ADD, "endBound" : BoundingType.UP_TO_SURFACE, "oppositeDirection" : true, "depth" : 25 * mm, "endBoundEntityFace" : qUnion([Q1]), "offsetDistance" : 25 * mm});
        }
        {
            var Q0;
            Q0=makeQuery(id+"F3.boolean.opBoolean","MERGE",FACE,{"derivedFrom":[makeQuery(id+"F1.opExtrude","SWEPT_FACE",FACE,{"disambiguationData":[OSD([sQuery(id+"F0.wireOp",EDGE,"E1.top")])]}),makeQuery(id+"F1.opExtrude","SWEPT_FACE",FACE,{"disambiguationData":[OSD([sQuery(id+"F0.wireOp",EDGE,"E109.trimOffspring")])]}),makeQuery(id+"F3.opExtrude","SWEPT_FACE",FACE,{"disambiguationData":[OSD([sQuery(id+"F2.wireOp",EDGE,"E110.2"),sQuery(id+"F2.wireOp",EDGE,"E110.111")])]})]});
            var sketch = newSketch(context, id + "F11", { "sketchPlane" : qUnion([Q0])});
            skLineSegment(sketch, "E143.bottom", {"start": v(-11870, 1300) * mm, "end": v(-10670, 1300) * mm});
            skLineSegment(sketch, "E143.top", {"start": v(-11870, 2200) * mm, "end": v(-10670, 2200) * mm});
            skLineSegment(sketch, "E143.left", {"start": v(-11870, 1300) * mm, "end": v(-11870, 2200) * mm});
            skLineSegment(sketch, "E143.right", {"start": v(-10670, 1300) * mm, "end": v(-10670, 2200) * mm});
            skLineSegment(sketch, "E144.bottom", {"start": v(-3800, 0) * mm, "end": v(-2200, 0) * mm});
            skLineSegment(sketch, "E144.top", {"start": v(-3800, 2200) * mm, "end": v(-2200, 2200) * mm});
            skLineSegment(sketch, "E144.left", {"start": v(-3800, 0) * mm, "end": v(-3800, 2200) * mm});
            skLineSegment(sketch, "E144.right", {"start": v(-2200, 0) * mm, "end": v(-2200, 1300) * mm});
            skLineSegment(sketch, "E145.bottom", {"start": v(-2200, 2200) * mm, "end": v(-700, 2200) * mm});
            skLineSegment(sketch, "E145.top", {"start": v(-2200, 1300) * mm, "end": v(-700, 1300) * mm});
            skLineSegment(sketch, "E145.right", {"start": v(-700, 2200) * mm, "end": v(-700, 1300) * mm});
            skSolve(sketch);
        }
        {
            var Q0;
            Q0 = qSketchRegion(id + "F11", true);
            extrude(context, id + "F12", {"entities" : qUnion([Q0]), "operationType" : NewBodyOperationType.REMOVE, "endBound" : BoundingType.UP_TO_NEXT, "oppositeDirection" : true, "depth" : 25 * mm, "offsetDistance" : 25 * mm});
        }
    });
